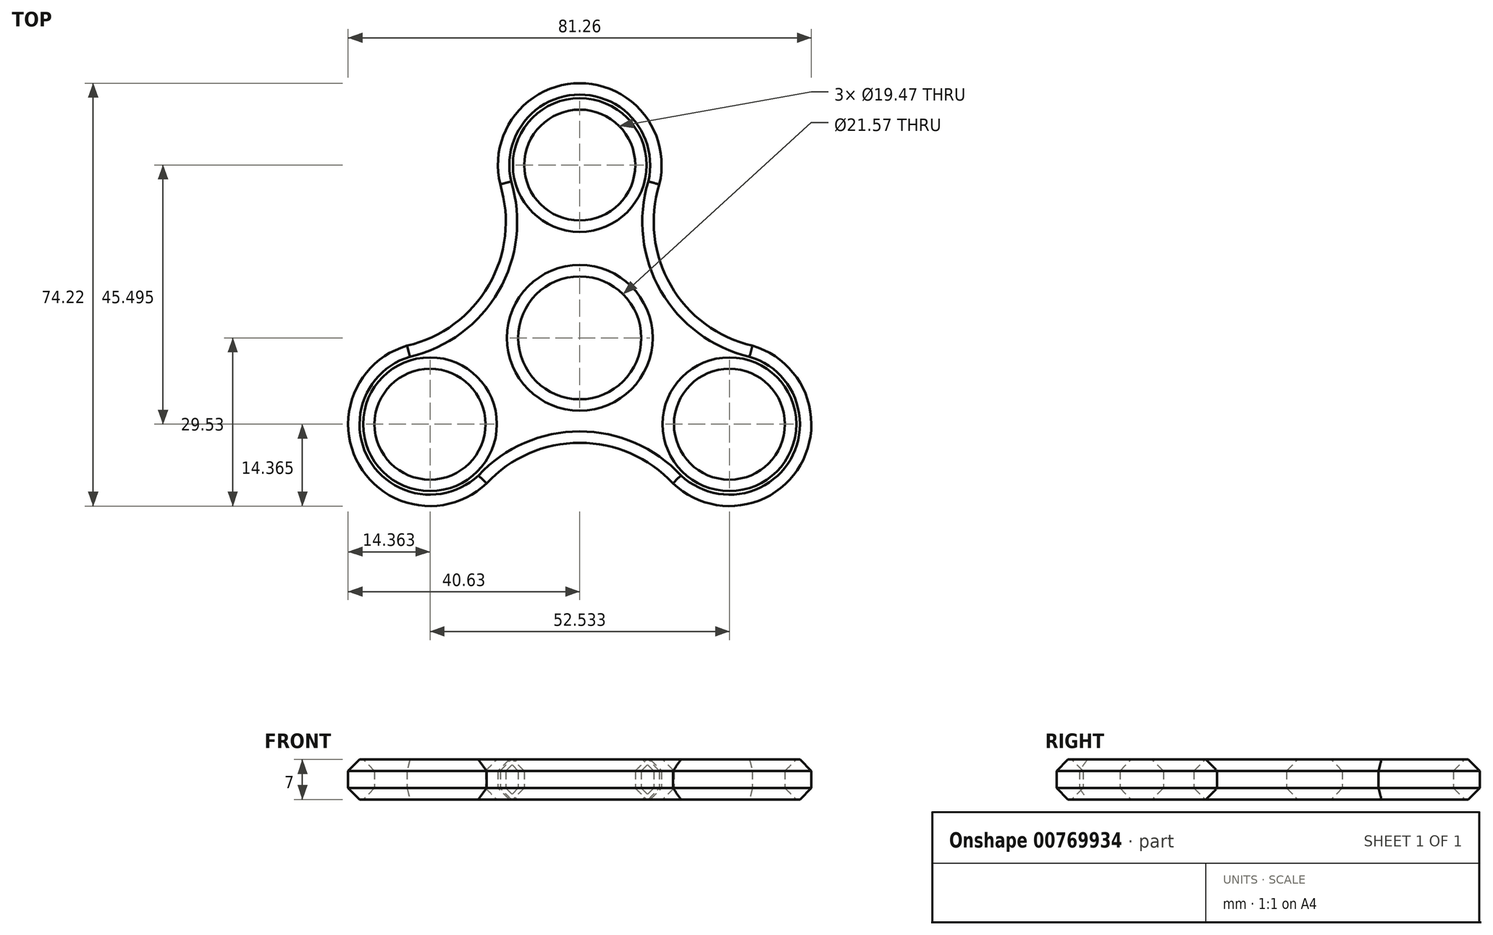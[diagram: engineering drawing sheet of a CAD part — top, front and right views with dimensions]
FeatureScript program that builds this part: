
annotation { "Feature Type Name" : "Feature", "Feature Type Description" : "" }
export const myFeature = defineFeature(function(context is Context, id is Id, definition is map)
    precondition{}
    {
        {
            var Q0;
            Q0=qCreatedBy(makeId("Top.planeOp"),FACE);
            var sketch = newSketch(context, id + "F0", { "sketchPlane" : qUnion([Q0])});
            skCircle(sketch, "E0", {"center": v(0, 30.33) * mm, "radius": 14.36 * mm});
            skCircle(sketch, "E1.1.0", {"center": v(-26.27, -15.17) * mm, "radius": 14.36 * mm});
            skCircle(sketch, "E1.2.0", {"center": v(26.27, -15.17) * mm, "radius": 14.36 * mm});
            skPoint(sketch, "E1.center", {"position": v(0, 0) * mm});
            skArc(sketch, "E2", {"start": v(-30.3, -1.38) * mm, "mid": v(-15.96, 9.21) * mm, "end": v(-13.95, 26.93) * mm});
            skArc(sketch, "E3.1.0", {"start": v(16.34, -25.55) * mm, "mid": v(0, -18.43) * mm, "end": v(-16.34, -25.55) * mm});
            skArc(sketch, "E3.2.0", {"start": v(13.95, 26.93) * mm, "mid": v(15.96, 9.21) * mm, "end": v(30.3, -1.38) * mm});
            skCircle(sketch, "E4", {"center": v(0, 30.33) * mm, "radius": 9.73 * mm});
            skCircle(sketch, "E5", {"center": v(0, 0) * mm, "radius": 10.79 * mm});
            skCircle(sketch, "E6.1.0", {"center": v(-26.27, -15.17) * mm, "radius": 9.73 * mm});
            skCircle(sketch, "E6.2.0", {"center": v(26.27, -15.17) * mm, "radius": 9.73 * mm});
            skSolve(sketch);
        }
        {
            var Q0;
            Q0=makeQuery(id+"F0.imprint","IMPRINT",FACE,{"disambiguationData":[TD([[makeQuery(id+"F0.imprint","IMPRINT",EDGE,{"derivedFrom":sQuery(id+"F0.wireOp",EDGE,"E5")}),-1.0]])]});
            var Q1;
            Q1=makeQuery(id+"F0.imprint","IMPRINT",FACE,{"disambiguationData":[TD([[makeQuery(id+"F0.imprint","IMPRINT",EDGE,{"derivedFrom":sQuery(id+"F0.wireOp",EDGE,"E4")}),-1.0]])]});
            var Q2;
            Q2=makeQuery(id+"F0.imprint","IMPRINT",FACE,{"disambiguationData":[TD([[makeQuery(id+"F0.imprint","IMPRINT",EDGE,{"derivedFrom":sQuery(id+"F0.wireOp",EDGE,"E6.2.0")}),-1.0]])]});
            var Q3;
            Q3=makeQuery(id+"F0.imprint","IMPRINT",FACE,{"disambiguationData":[TD([[makeQuery(id+"F0.imprint","IMPRINT",EDGE,{"derivedFrom":sQuery(id+"F0.wireOp",EDGE,"E6.1.0")}),-1.0]])]});
            extrude(context, id + "F1", {"entities" : qUnion([Q0, Q1, Q2, Q3]), "depth" : 7 * mm, "offsetDistance" : 25 * mm});
        }
        {
            var Q0;
            Q0=makeQuery(id+"F1.opExtrude","CAP_EDGE",EDGE,{"disambiguationData":[OSD([sQuery(id+"F0.wireOp",EDGE,"E1.1.0")])],"isStart":false});
            var Q1;
            Q1=makeQuery(id+"F1.opExtrude","CAP_EDGE",EDGE,{"disambiguationData":[OSD([sQuery(id+"F0.wireOp",EDGE,"E2")])],"isStart":false});
            var Q2;
            Q2=makeQuery(id+"F1.opExtrude","CAP_EDGE",EDGE,{"disambiguationData":[OSD([sQuery(id+"F0.wireOp",EDGE,"E0")])],"isStart":false});
            var Q3;
            Q3=makeQuery(id+"F1.opExtrude","CAP_EDGE",EDGE,{"disambiguationData":[OSD([sQuery(id+"F0.wireOp",EDGE,"E4")])],"isStart":false});
            var Q4;
            Q4=makeQuery(id+"F1.opExtrude","CAP_EDGE",EDGE,{"disambiguationData":[OSD([sQuery(id+"F0.wireOp",EDGE,"E5")])],"isStart":false});
            var Q5;
            Q5=makeQuery(id+"F1.opExtrude","CAP_EDGE",EDGE,{"disambiguationData":[OSD([sQuery(id+"F0.wireOp",EDGE,"E6.2.0")])],"isStart":false});
            var Q6;
            Q6=makeQuery(id+"F1.opExtrude","CAP_EDGE",EDGE,{"disambiguationData":[OSD([sQuery(id+"F0.wireOp",EDGE,"E6.1.0")])],"isStart":false});
            var Q7;
            Q7=makeQuery(id+"F1.opExtrude","CAP_EDGE",EDGE,{"disambiguationData":[OSD([sQuery(id+"F0.wireOp",EDGE,"E3.1.0")])],"isStart":false});
            var Q8;
            Q8=makeQuery(id+"F1.opExtrude","CAP_EDGE",EDGE,{"disambiguationData":[OSD([sQuery(id+"F0.wireOp",EDGE,"E1.2.0")])],"isStart":false});
            var Q9;
            Q9=makeQuery(id+"F1.opExtrude","CAP_EDGE",EDGE,{"disambiguationData":[OSD([sQuery(id+"F0.wireOp",EDGE,"E3.2.0")])],"isStart":false});
            chamfer(context, id + "F2", {"entities" : qUnion([Q0, Q1, Q2, Q3, Q4, Q5, Q6, Q7, Q8, Q9]), "width" : 2 * mm, "tangentPropagation" : true});
        }
        {
            var Q0;
            Q0=makeQuery(id+"F1.opExtrude","CAP_EDGE",EDGE,{"disambiguationData":[OSD([sQuery(id+"F0.wireOp",EDGE,"E1.1.0")])],"isStart":true});
            var Q1;
            Q1=makeQuery(id+"F1.opExtrude","CAP_EDGE",EDGE,{"disambiguationData":[OSD([sQuery(id+"F0.wireOp",EDGE,"E3.1.0")])],"isStart":true});
            var Q2;
            Q2=makeQuery(id+"F1.opExtrude","CAP_EDGE",EDGE,{"disambiguationData":[OSD([sQuery(id+"F0.wireOp",EDGE,"E1.2.0")])],"isStart":true});
            var Q3;
            Q3=makeQuery(id+"F1.opExtrude","CAP_EDGE",EDGE,{"disambiguationData":[OSD([sQuery(id+"F0.wireOp",EDGE,"E6.2.0")])],"isStart":true});
            var Q4;
            Q4=makeQuery(id+"F1.opExtrude","CAP_EDGE",EDGE,{"disambiguationData":[OSD([sQuery(id+"F0.wireOp",EDGE,"E3.2.0")])],"isStart":true});
            var Q5;
            Q5=makeQuery(id+"F1.opExtrude","CAP_EDGE",EDGE,{"disambiguationData":[OSD([sQuery(id+"F0.wireOp",EDGE,"E0")])],"isStart":true});
            var Q6;
            Q6=makeQuery(id+"F1.opExtrude","CAP_FACE",FACE,{"disambiguationData":[OSD([sQuery(id+"F0.wireOp",EDGE,"E0"),sQuery(id+"F0.wireOp",EDGE,"E1.1.0"),sQuery(id+"F0.wireOp",EDGE,"E1.2.0"),sQuery(id+"F0.wireOp",EDGE,"E2"),sQuery(id+"F0.wireOp",EDGE,"E3.1.0"),sQuery(id+"F0.wireOp",EDGE,"E3.2.0"),sQuery(id+"F0.wireOp",EDGE,"E4"),sQuery(id+"F0.wireOp",EDGE,"E5"),sQuery(id+"F0.wireOp",EDGE,"E6.1.0"),sQuery(id+"F0.wireOp",EDGE,"E6.2.0")])],"isStart":true});
            chamfer(context, id + "F3", {"entities" : qUnion([Q0, Q1, Q2, Q3, Q4, Q5, Q6]), "width" : 2 * mm, "tangentPropagation" : true});
        }
    });
